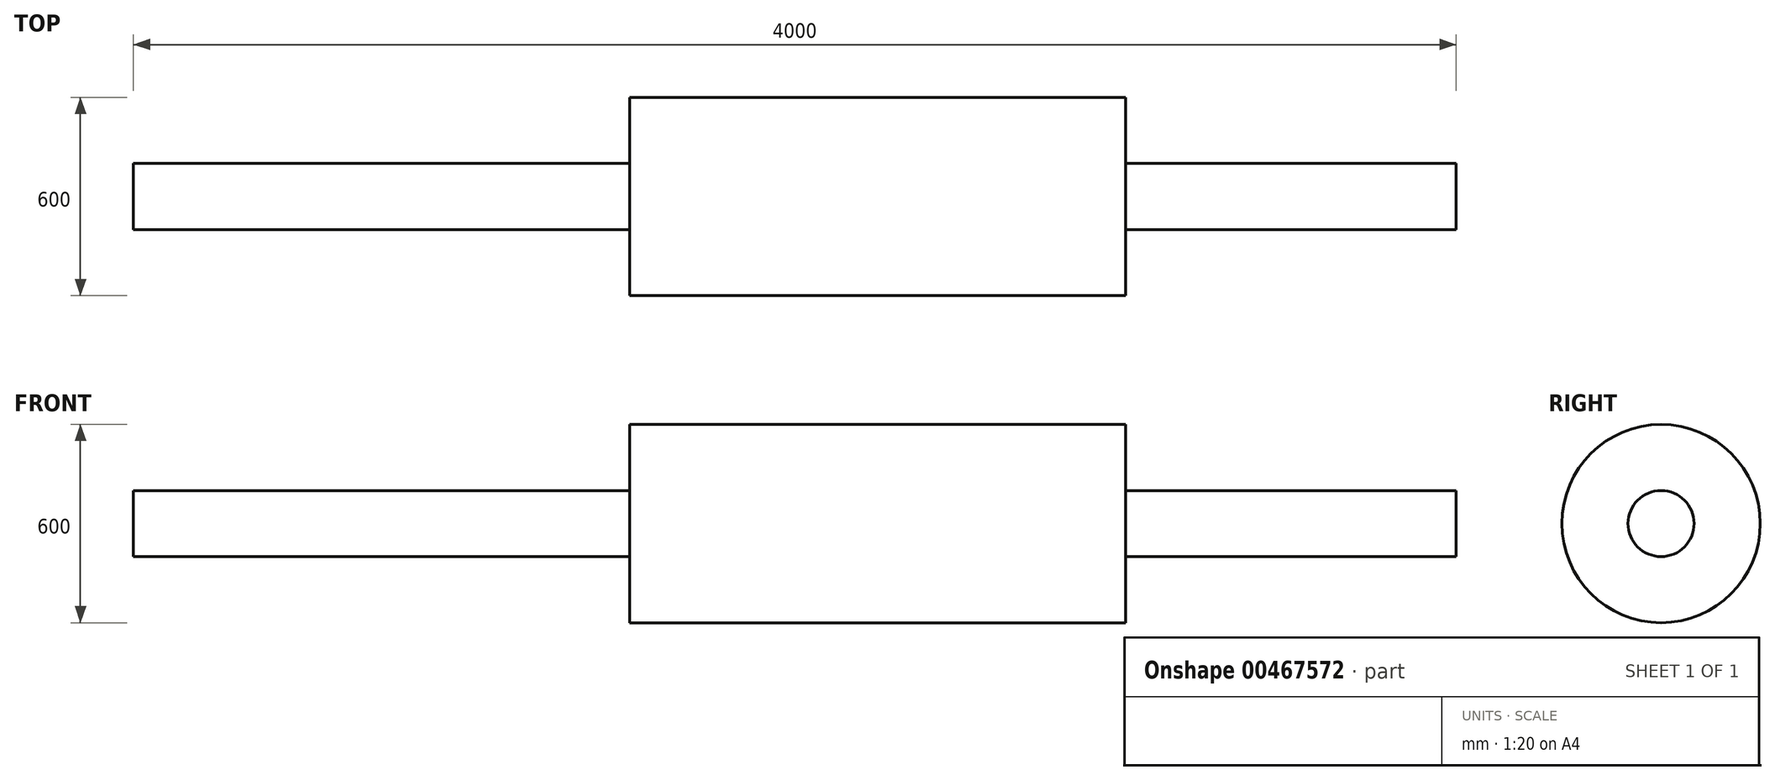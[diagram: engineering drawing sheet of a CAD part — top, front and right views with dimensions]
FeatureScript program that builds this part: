
annotation { "Feature Type Name" : "Feature", "Feature Type Description" : "" }
export const myFeature = defineFeature(function(context is Context, id is Id, definition is map)
    precondition{}
    {
        {
            var Q0;
            Q0=qCreatedBy(makeId("Front.planeOp"),FACE);
            var sketch = newSketch(context, id + "F0", { "sketchPlane" : qUnion([Q0])});
            skLineSegment(sketch, "E0", {"start": v(0, 0) * mm, "end": v(0, 100) * mm});
            skLineSegment(sketch, "E1", {"start": v(0, 100) * mm, "end": v(1500, 100) * mm});
            skLineSegment(sketch, "E2", {"start": v(1500, 100) * mm, "end": v(1500, 300) * mm});
            skLineSegment(sketch, "E3", {"start": v(1500, 300) * mm, "end": v(3000, 300) * mm});
            skLineSegment(sketch, "E4.MirrorCS", {"start": v(4000, 0) * mm, "end": v(4000, 100) * mm});
            skLineSegment(sketch, "E5.MirrorCS", {"start": v(3000, 100) * mm, "end": v(3000, 300) * mm});
            skLineSegment(sketch, "E6.MirrorCS", {"start": v(4000, 100) * mm, "end": v(3000, 100) * mm});
            skLineSegment(sketch, "E7", {"start": v(0, 0) * mm, "end": v(4000, 0) * mm});
            skLineSegment(sketch, "E8", {"start": v(-1096.07, 0) * mm, "end": v(5129.2, 0) * mm, "construction": true});
            skSolve(sketch);
        }
        {
            var Q0;
            Q0 = qSketchRegion(id + "F0", true);
            var Q1;
            Q1=sQuery(id+"F0.wireOp",EDGE,"E7");
            revolve(context, id + "F1", {"entities" : qUnion([Q0]), "axis" : qUnion([Q1]), "revolveType" : RevolveType.FULL});
        }
    });
